# Revit family: Haworth_Massimosistema_Ottoman
name_source: partatom
category: Furniture
revit_build: Autodesk Revit 2018 (Build: 20170223_1515(x64)
units: mm (PartAtom-declared; Revit-internal decimal feet)

## family parameters
Always vertical = Yes
Cut with Voids When Loaded = No
OmniClass Number = 23.40.20.00
OmniClass Title = General Furniture and Specialties
Room Calculation Point = No
Shared = No
Work Plane-Based = No

## types (2) — shared parameters
Actual Height = 16 1/2"
Assembly Code = E2020200
Frame Finish = Haworth _ Paint _ Metallic Gunmetal
Manufacturer = Haworth
Size = Verify Final Dim. w/ Haworth
URL = http://www.haworth.com
URL - Product = http://www.haworth.com
Version = 1
Warranty = https://www.haworth.com

## per-type parameters (varying)
| type | Actual Depth | Actual Width | Description | Large | Small |
| HCPF-MSFL | 50 1/2" | 50 1/2" | Haworth Massimosistema Sofa - Large Ottoman | Yes | No |
| HCPF-MSFS | 33 1/2" | 33 1/2" | Haworth Massimosistema Sofa - Small Ottoman | No | Yes |

note: column(s) folded — value = type name in every type: Model

## geometry (parser evidence)
native form markers: Sweep x3
no freeform markers — native parametric forms only
